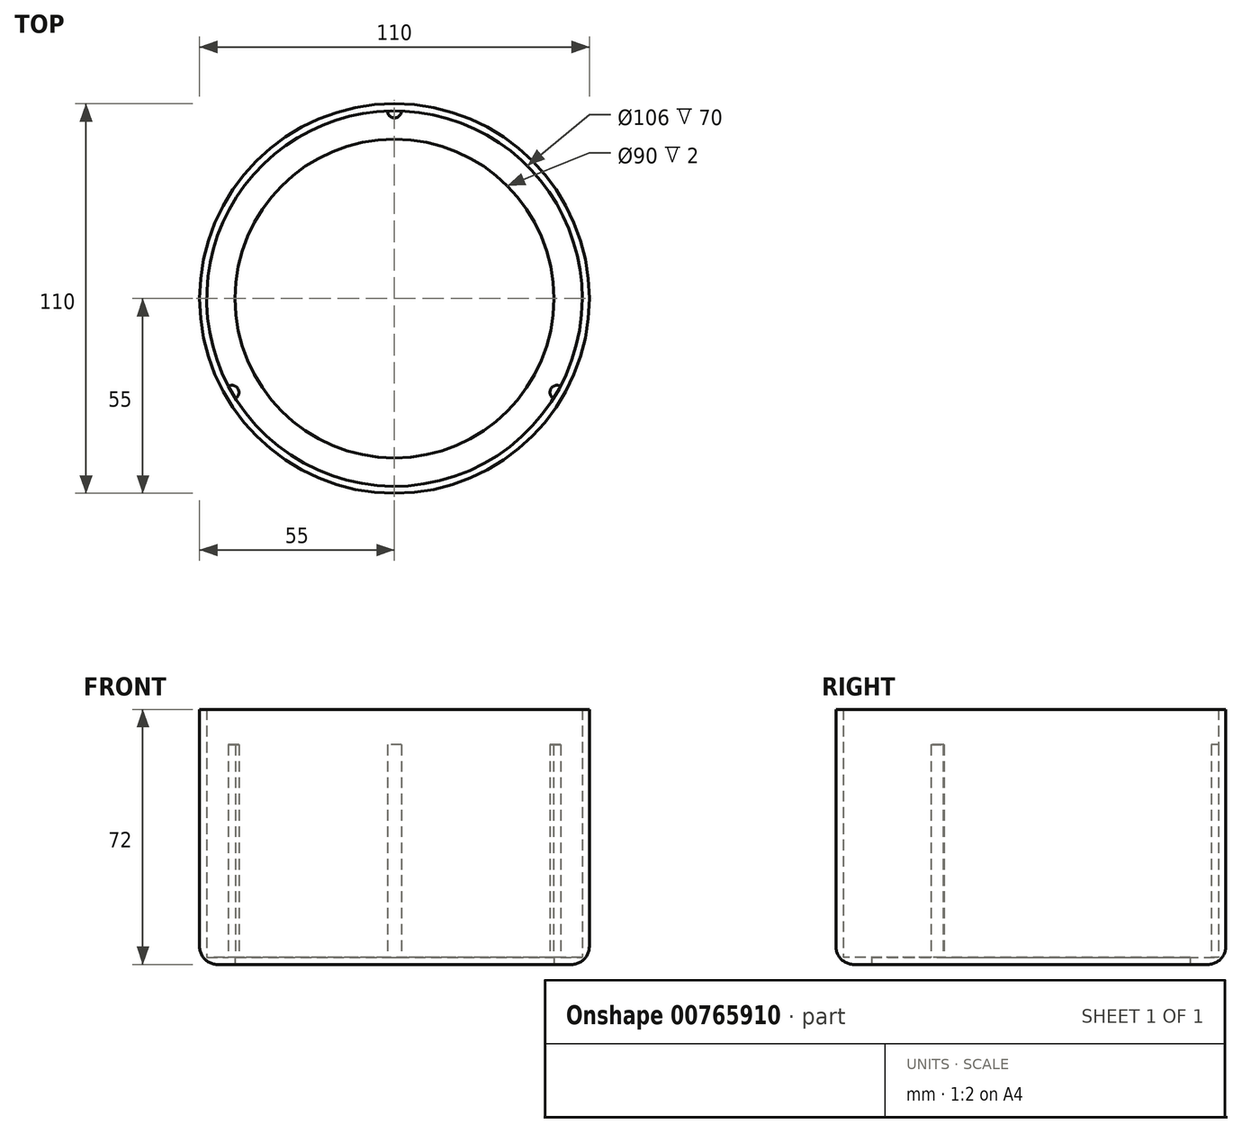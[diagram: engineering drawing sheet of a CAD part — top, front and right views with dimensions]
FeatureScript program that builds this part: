
annotation { "Feature Type Name" : "Feature", "Feature Type Description" : "" }
export const myFeature = defineFeature(function(context is Context, id is Id, definition is map)
    precondition{}
    {
        {
            var Q0;
            Q0=qCreatedBy(makeId("Top.planeOp"),FACE);
            var sketch = newSketch(context, id + "F0", { "sketchPlane" : qUnion([Q0])});
            skCircle(sketch, "E0", {"center": v(0, 0) * mm, "radius": 55 * mm});
            skCircle(sketch, "E1", {"center": v(0, 0) * mm, "radius": 45 * mm});
            skSolve(sketch);
        }
        {
            var Q0;
            Q0=makeQuery(id+"F0.imprint","IMPRINT",FACE,{"disambiguationData":[TD([[makeQuery(id+"F0.imprint","IMPRINT",EDGE,{"derivedFrom":sQuery(id+"F0.wireOp",EDGE,"E1")}),-1.0]])]});
            var Q1;
            Q1=makeQuery(id+"F0.imprint","IMPRINT",FACE,{"disambiguationData":[TD([[makeQuery(id+"F0.imprint","IMPRINT",EDGE,{"derivedFrom":sQuery(id+"F0.wireOp",EDGE,"E0")}),1.0]])]});
            extrude(context, id + "F1", {"entities" : qUnion([Q0, Q1]), "depth" : 2 * mm, "offsetDistance" : 25 * mm});
        }
        {
            var Q0;
            Q0=makeQuery(id+"F1.opExtrude","CAP_FACE",FACE,{"disambiguationData":[OSD([sQuery(id+"F0.wireOp",EDGE,"E0"),sQuery(id+"F0.wireOp",EDGE,"E1")])],"isStart":false});
            var sketch = newSketch(context, id + "F2", { "sketchPlane" : qUnion([Q0])});
            skCircle(sketch, "E2.0", {"center": v(0, 0) * mm, "radius": 53 * mm});
            skSolve(sketch);
        }
        {
            var Q0;
            Q0=makeQuery(id+"F2.imprint","IMPRINT",FACE,{"disambiguationData":[TD([[makeQuery(id+"F2.imprint","IMPRINT",EDGE,{"derivedFrom":sQuery(id+"F2.wireOp",EDGE,"E2.0")}),-1.0]])]});
            extrude(context, id + "F3", {"entities" : qUnion([Q0]), "operationType" : NewBodyOperationType.ADD, "depth" : 70 * mm, "offsetDistance" : 25 * mm});
        }
        {
            var Q0;
            Q0=makeQuery(id+"F1.opExtrude","CAP_FACE",FACE,{"disambiguationData":[OSD([sQuery(id+"F0.wireOp",EDGE,"E0"),sQuery(id+"F0.wireOp",EDGE,"E1")])],"isStart":false});
            var sketch = newSketch(context, id + "F4", { "sketchPlane" : qUnion([Q0])});
            skArc(sketch, "E3", {"start": v(-2, 52.96) * mm, "mid": v(0, 51) * mm, "end": v(2, 52.96) * mm});
            skPoint(sketch, "E4.center", {"position": v(0, 0.89) * mm});
            skArc(sketch, "E5.1.0", {"start": v(-44.87, -28.21) * mm, "mid": v(-44.17, -25.5) * mm, "end": v(-46.87, -24.75) * mm});
            skArc(sketch, "E5.2.0", {"start": v(46.87, -24.75) * mm, "mid": v(44.17, -25.5) * mm, "end": v(44.87, -28.21) * mm});
            skPoint(sketch, "E5.center", {"position": v(0, 0) * mm});
            skSolve(sketch);
        }
        {
            var Q0;
            {var subQ0=sQuery(id+"F4.wireOp",EDGE,"E3");Q0=makeQuery(id+"F4.imprint","IMPRINT",FACE,{"disambiguationData":[TD([[makeQuery(id+"F4.imprint","IMPRINT",EDGE,{"derivedFrom":subQ0}),1.0]])]});}
            var Q1;
            {var subQ0=sQuery(id+"F4.wireOp",EDGE,"E5.2.0");Q1=makeQuery(id+"F4.imprint","IMPRINT",FACE,{"disambiguationData":[TD([[makeQuery(id+"F4.imprint","IMPRINT",EDGE,{"derivedFrom":subQ0}),1.0]])]});}
            var Q2;
            {var subQ0=sQuery(id+"F4.wireOp",EDGE,"E5.1.0");Q2=makeQuery(id+"F4.imprint","IMPRINT",FACE,{"disambiguationData":[TD([[makeQuery(id+"F4.imprint","IMPRINT",EDGE,{"derivedFrom":subQ0}),1.0]])]});}
            var Q3;
            Q3=makeQuery(id+"F3.opExtrude","CAP_FACE",FACE,{"disambiguationData":[OSD([sQuery(id+"F0.wireOp",EDGE,"E0"),sQuery(id+"F2.wireOp",EDGE,"E2.0")])],"isStart":false});
            extrude(context, id + "F5", {"entities" : qUnion([Q0, Q1, Q2]), "operationType" : NewBodyOperationType.ADD, "endBound" : BoundingType.UP_TO_SURFACE, "depth" : 25 * mm, "endBoundEntityFace" : qUnion([Q3]), "hasOffset" : true, "offsetDistance" : 10 * mm});
        }
        {
            var Q0;
            Q0=makeQuery(id+"F1.opExtrude","CAP_EDGE",EDGE,{"disambiguationData":[OSD([sQuery(id+"F0.wireOp",EDGE,"E0")])],"isStart":true});
            fillet(context, id + "F6", {"entities" : qUnion([Q0]), "radius" : 5 * mm, "tangentPropagation" : true, "allowEdgeOverflow" : false});
        }
    });
